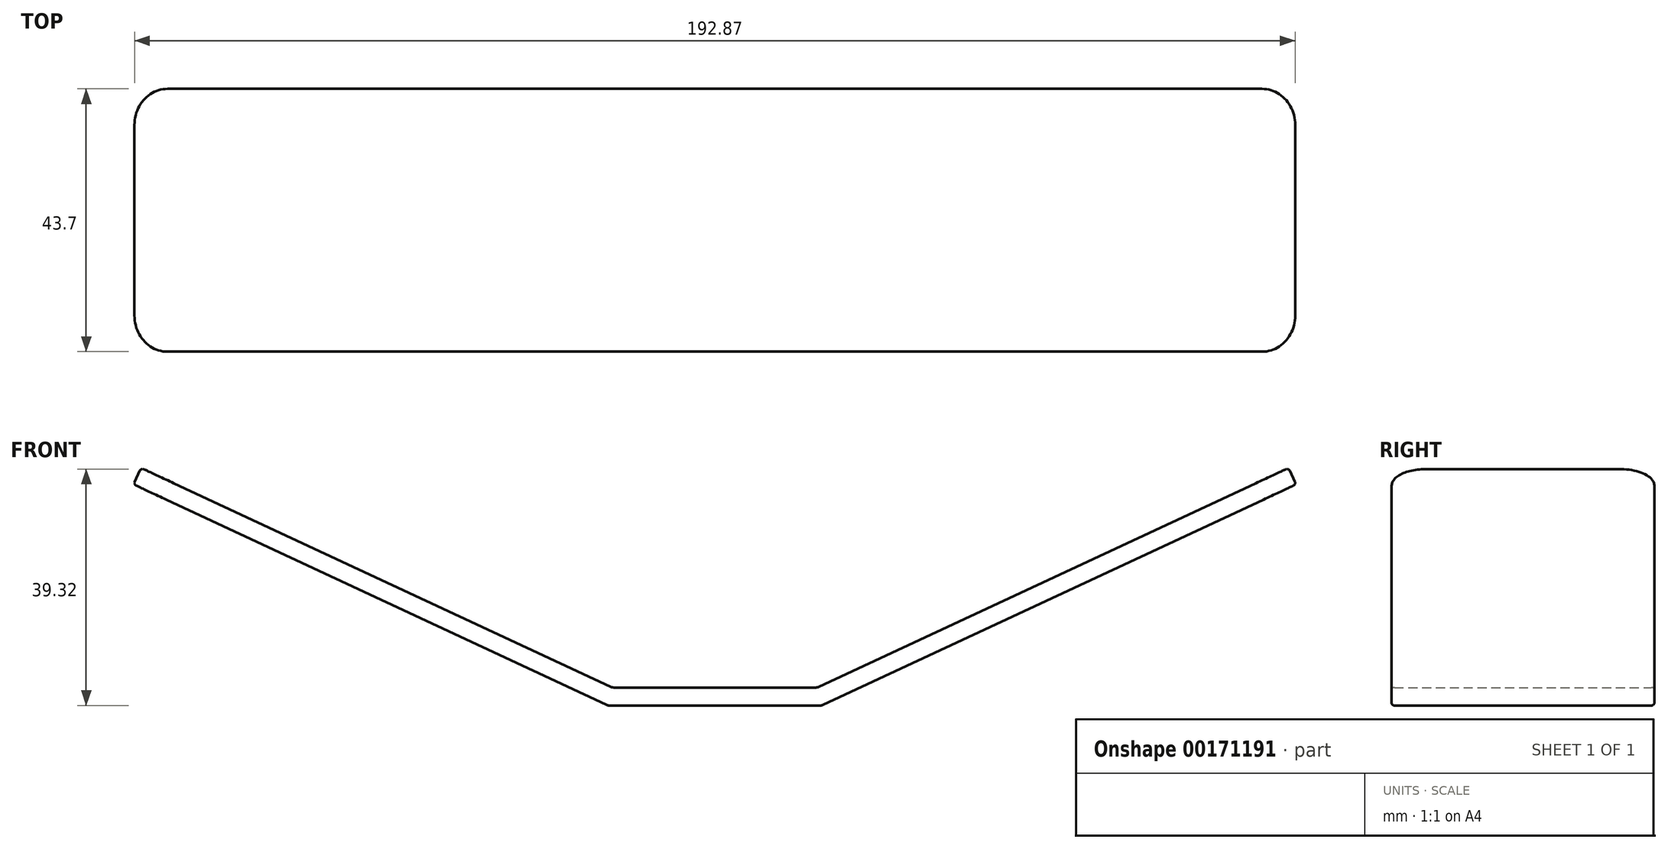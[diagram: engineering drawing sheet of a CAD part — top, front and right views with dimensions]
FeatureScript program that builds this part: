
annotation { "Feature Type Name" : "Feature", "Feature Type Description" : "" }
export const myFeature = defineFeature(function(context is Context, id is Id, definition is map)
    precondition{}
    {
        {
            var Q0;
            Q0=qCreatedBy(makeId("Front.planeOp"),FACE);
            var sketch = newSketch(context, id + "F0", { "sketchPlane" : qUnion([Q0])});
            skLineSegment(sketch, "E0", {"start": v(17.77, 0) * mm, "end": v(53.4, 0) * mm, "construction": true});
            skLineSegment(sketch, "E1", {"start": v(17.77, 0) * mm, "end": v(96.62, 36.77) * mm, "construction": true});
            skLineSegment(sketch, "E2", {"start": v(17.77, 0) * mm, "end": v(96.62, 36.77) * mm});
            skLineSegment(sketch, "E3", {"start": v(-17.73, 0) * mm, "end": v(-67.88, 0) * mm, "construction": true});
            skLineSegment(sketch, "E4", {"start": v(-17.73, 0) * mm, "end": v(-96.58, 36.77) * mm, "construction": true});
            skLineSegment(sketch, "E5", {"start": v(-17.73, 0) * mm, "end": v(-96.58, 36.77) * mm});
            skLineSegment(sketch, "E6.0", {"start": v(-17.06, 3) * mm, "end": v(17.1, 3) * mm});
            skLineSegment(sketch, "E7.0", {"start": v(17.1, 3) * mm, "end": v(95.35, 39.49) * mm});
            skLineSegment(sketch, "E8.0", {"start": v(-17.06, 3) * mm, "end": v(-95.31, 39.49) * mm});
            skLineSegment(sketch, "E9", {"start": v(96.62, 36.77) * mm, "end": v(95.35, 39.49) * mm});
            skLineSegment(sketch, "E10", {"start": v(-96.58, 36.77) * mm, "end": v(-95.31, 39.49) * mm});
            skLineSegment(sketch, "E11", {"start": v(-17.73, 0) * mm, "end": v(17.77, 0) * mm});
            skSolve(sketch);
        }
        {
            var Q0;
            Q0=makeQuery(id+"F0.imprint","IMPRINT",FACE,{"disambiguationData":[TD([[makeQuery(id+"F0.imprint","IMPRINT",EDGE,{"derivedFrom":sQuery(id+"F0.wireOp",EDGE,"E2")}),1.0]])]});
            extrude(context, id + "F1", {"entities" : qUnion([Q0]), "depth" : 43.7 * mm});
        }
        {
            var Q0;
            Q0=makeQuery(id+"F1.opExtrude","CAP_EDGE",EDGE,{"disambiguationData":[OSD([sQuery(id+"F0.wireOp",EDGE,"E10")])],"isStart":false});
            var Q1;
            Q1=makeQuery(id+"F1.opExtrude","CAP_EDGE",EDGE,{"disambiguationData":[OSD([sQuery(id+"F0.wireOp",EDGE,"E10")])],"isStart":true});
            var Q2;
            Q2=makeQuery(id+"F1.opExtrude","CAP_EDGE",EDGE,{"disambiguationData":[OSD([sQuery(id+"F0.wireOp",EDGE,"E9")])],"isStart":true});
            var Q3;
            Q3=makeQuery(id+"F1.opExtrude","CAP_EDGE",EDGE,{"disambiguationData":[OSD([sQuery(id+"F0.wireOp",EDGE,"E9")])],"isStart":false});
            fillet(context, id + "F2", {"entities" : qUnion([Q0, Q1, Q2, Q3]), "radius" : 6 * mm, "tangentPropagation" : true, "allowEdgeOverflow" : false});
        }
        {
            var Q0;
            Q0=makeQuery(id+"F1.opExtrude","SWEPT_EDGE",EDGE,{"disambiguationData":[OSD([sQuery(id+"F0.wireOp",EDGE,"E2"),sQuery(id+"F0.wireOp",EDGE,"E11")])]});
            var Q1;
            Q1=makeQuery(id+"F1.opExtrude","SWEPT_EDGE",EDGE,{"disambiguationData":[OSD([sQuery(id+"F0.wireOp",EDGE,"E5"),sQuery(id+"F0.wireOp",EDGE,"E11")])]});
            var Q2;
            Q2=makeQuery(id+"F1.opExtrude","SWEPT_EDGE",EDGE,{"disambiguationData":[OSD([sQuery(id+"F0.wireOp",EDGE,"E6.0"),sQuery(id+"F0.wireOp",EDGE,"E7.0")])]});
            var Q3;
            Q3=makeQuery(id+"F1.opExtrude","SWEPT_EDGE",EDGE,{"disambiguationData":[OSD([sQuery(id+"F0.wireOp",EDGE,"E6.0"),sQuery(id+"F0.wireOp",EDGE,"E8.0")])]});
            fillet(context, id + "F3", {"entities" : qUnion([Q0, Q1, Q2, Q3]), "radius" : 1 * mm, "tangentPropagation" : true, "allowEdgeOverflow" : false});
        }
        {
            var Q0;
            Q0=makeQuery(id+"F1.opExtrude","CAP_EDGE",EDGE,{"disambiguationData":[OSD([sQuery(id+"F0.wireOp",EDGE,"E8.0")])],"isStart":true});
            var Q1;
            Q1=makeQuery(id+"F1.opExtrude","CAP_EDGE",EDGE,{"disambiguationData":[OSD([sQuery(id+"F0.wireOp",EDGE,"E6.0")])],"isStart":true});
            var Q2;
            Q2=makeQuery(id+"F1.opExtrude","SWEPT_FACE",FACE,{"disambiguationData":[OSD([sQuery(id+"F0.wireOp",EDGE,"E5")])]});
            fillet(context, id + "F4", {"entities" : qUnion([Q0, Q1, Q2]), "radius" : 0.5 * mm, "tangentPropagation" : true, "allowEdgeOverflow" : false});
        }
    });
